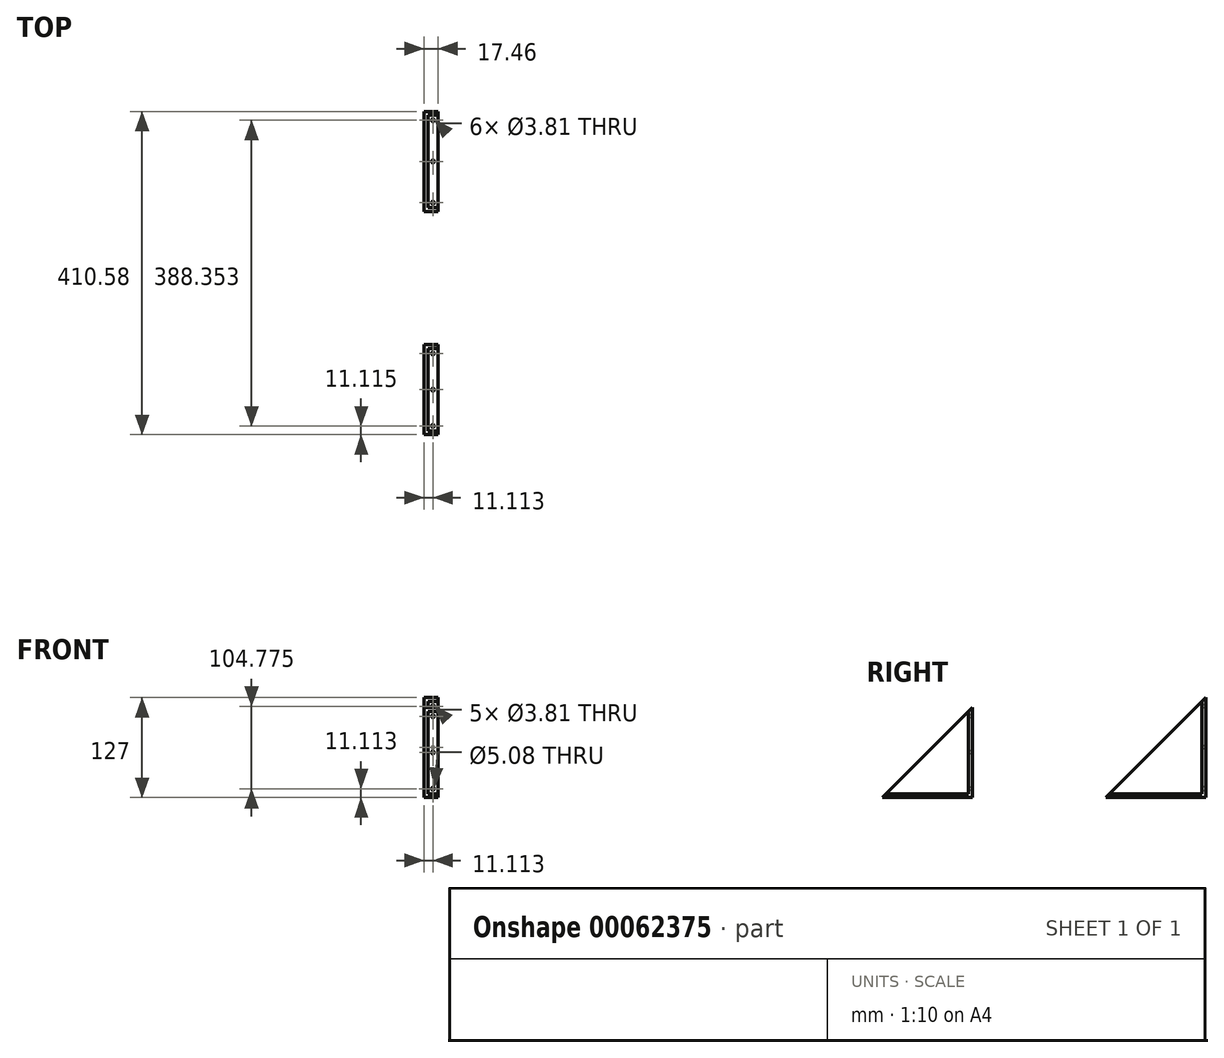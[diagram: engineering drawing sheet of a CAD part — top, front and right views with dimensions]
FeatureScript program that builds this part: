
annotation { "Feature Type Name" : "Feature", "Feature Type Description" : "" }
export const myFeature = defineFeature(function(context is Context, id is Id, definition is map)
    precondition{}
    {
        {
            var Q0;
            Q0=qCreatedBy(makeId("Right.planeOp"),FACE);
            var sketch = newSketch(context, id + "F0", { "sketchPlane" : qUnion([Q0])});
            skLineSegment(sketch, "E0", {"start": v(0, 0) * mm, "end": v(127, 127) * mm});
            skLineSegment(sketch, "E1", {"start": v(127, 127) * mm, "end": v(127, 0) * mm});
            skLineSegment(sketch, "E2", {"start": v(127, 0) * mm, "end": v(0, 0) * mm});
            skSolve(sketch);
        }
        {
            var Q0;
            Q0=makeQuery(id+"F0.imprint","IMPRINT",FACE,{"disambiguationData":[TD([[makeQuery(id+"F0.imprint","IMPRINT",EDGE,{"derivedFrom":sQuery(id+"F0.wireOp",EDGE,"E0")}),-1.0]])]});
            extrude(context, id + "F1", {"entities" : qUnion([Q0]), "depth" : 4.76 * mm});
        }
        {
            var Q0;
            Q0=makeQuery(id+"F1.opExtrude","CAP_FACE",FACE,{"disambiguationData":[OSD([sQuery(id+"F0.wireOp",EDGE,"E0"),sQuery(id+"F0.wireOp",EDGE,"E1"),sQuery(id+"F0.wireOp",EDGE,"E2")])],"isStart":false});
            var sketch = newSketch(context, id + "F2", { "sketchPlane" : qUnion([Q0])});
            skLineSegment(sketch, "E3", {"start": v(127, 4.76) * mm, "end": v(4.76, 4.76) * mm});
            skLineSegment(sketch, "E4", {"start": v(122.24, 4.76) * mm, "end": v(122.24, 122.24) * mm});
            skSolve(sketch);
        }
        {
            var Q0;
            {var subQ3=sQuery(id+"F2.wireOp",EDGE,"E4");Q0=makeQuery(id+"F2.imprint","IMPRINT",FACE,{"disambiguationData":[TD([[makeQuery(id+"F2.imprint","IMPRINT",EDGE,{"derivedFrom":subQ3}),-1.0]])]});}
            var Q1;
            {var subQ0=makeQuery(id+"F1.opExtrude","CAP_EDGE",EDGE,{"disambiguationData":[OSD([sQuery(id+"F0.wireOp",EDGE,"E2")])],"isStart":false});Q1=makeQuery(id+"F2.imprint","IMPRINT",FACE,{"disambiguationData":[TD([[makeQuery(id+"F2.imprint","IMPRINT",EDGE,{"derivedFrom":subQ0}),-1.0]])]});}
            extrude(context, id + "F3", {"entities" : qUnion([Q0, Q1]), "operationType" : NewBodyOperationType.ADD, "depth" : 12.7 * mm});
        }
        {
            var Q0;
            Q0=makeQuery(id+"F3.opExtrude","SWEPT_FACE",FACE,{"disambiguationData":[OSD([sQuery(id+"F2.wireOp",EDGE,"E3")])]});
            var sketch = newSketch(context, id + "F4", { "sketchPlane" : qUnion([Q0])});
            skCircle(sketch, "E5", {"center": v(11.11, 11.11) * mm, "radius": 1.9 * mm});
            skPoint(sketch, "E5.centerSnap0", {"position": v(11.11, 4.76) * mm});
            skCircle(sketch, "E6", {"center": v(11.11, 115.89) * mm, "radius": 1.9 * mm});
            skCircle(sketch, "E7", {"center": v(11.11, 63.5) * mm, "radius": 1.9 * mm});
            skPoint(sketch, "E7.centerSnap0", {"position": v(17.46, 63.5) * mm});
            skSolve(sketch);
        }
        {
            var Q0;
            Q0=qSketchRegion(id+"F4",true);
            extrude(context, id + "F5", {"entities" : qUnion([Q0]), "operationType" : NewBodyOperationType.REMOVE, "endBound" : BoundingType.UP_TO_NEXT, "oppositeDirection" : true, "depth" : 25.4 * mm});
        }
        {
            var Q0;
            Q0=makeQuery(id+"F3.opExtrude","SWEPT_FACE",FACE,{"disambiguationData":[OSD([sQuery(id+"F2.wireOp",EDGE,"E4")])]});
            var sketch = newSketch(context, id + "F6", { "sketchPlane" : qUnion([Q0])});
            skCircle(sketch, "E8", {"center": v(11.11, 115.89) * mm, "radius": 1.9 * mm});
            skPoint(sketch, "E8.centerSnap0", {"position": v(11.11, 122.24) * mm});
            skCircle(sketch, "E9", {"center": v(11.11, 11.11) * mm, "radius": 2.54 * mm});
            skCircle(sketch, "E10", {"center": v(11.11, 63.5) * mm, "radius": 1.9 * mm});
            skPoint(sketch, "E10.centerSnap0", {"position": v(17.46, 63.5) * mm});
            skSolve(sketch);
        }
        {
            var Q0;
            Q0=makeQuery(id+"F6.imprint","IMPRINT",FACE,{"disambiguationData":[TD([[makeQuery(id+"F6.imprint","IMPRINT",EDGE,{"derivedFrom":sQuery(id+"F6.wireOp",EDGE,"E8")}),1.0]])]});
            var Q1;
            Q1=makeQuery(id+"F6.imprint","IMPRINT",FACE,{"disambiguationData":[TD([[makeQuery(id+"F6.imprint","IMPRINT",EDGE,{"derivedFrom":sQuery(id+"F6.wireOp",EDGE,"E9")}),1.0]])]});
            var Q2;
            Q2=makeQuery(id+"F6.imprint","IMPRINT",FACE,{"disambiguationData":[TD([[makeQuery(id+"F6.imprint","IMPRINT",EDGE,{"derivedFrom":sQuery(id+"F6.wireOp",EDGE,"E10")}),1.0]])]});
            extrude(context, id + "F7", {"entities" : qUnion([Q0, Q1, Q2]), "operationType" : NewBodyOperationType.REMOVE, "endBound" : BoundingType.UP_TO_NEXT, "oppositeDirection" : true, "depth" : 25.4 * mm});
        }
        {
            var Q0;
            Q0=qCreatedBy(makeId("Right.planeOp"),FACE);
            var sketch = newSketch(context, id + "F8", { "sketchPlane" : qUnion([Q0])});
            skLineSegment(sketch, "E11", {"start": v(-283.58, 0) * mm, "end": v(-169.28, 114.3) * mm});
            skLineSegment(sketch, "E12", {"start": v(-169.28, 114.3) * mm, "end": v(-169.28, 0) * mm});
            skLineSegment(sketch, "E13", {"start": v(-169.28, 0) * mm, "end": v(-283.58, 0) * mm});
            skSolve(sketch);
        }
        {
            var Q0;
            Q0=makeQuery(id+"F8.imprint","IMPRINT",FACE,{"disambiguationData":[TD([[makeQuery(id+"F8.imprint","IMPRINT",EDGE,{"derivedFrom":sQuery(id+"F8.wireOp",EDGE,"E11")}),-1.0]])]});
            extrude(context, id + "F9", {"entities" : qUnion([Q0]), "depth" : 4.76 * mm});
        }
        {
            var Q0;
            Q0=makeQuery(id+"F9.opExtrude","CAP_FACE",FACE,{"disambiguationData":[OSD([sQuery(id+"F8.wireOp",EDGE,"E11"),sQuery(id+"F8.wireOp",EDGE,"E12"),sQuery(id+"F8.wireOp",EDGE,"E13")])],"isStart":false});
            var sketch = newSketch(context, id + "F10", { "sketchPlane" : qUnion([Q0])});
            skLineSegment(sketch, "E14", {"start": v(-278.82, 4.76) * mm, "end": v(-169.28, 4.76) * mm});
            skLineSegment(sketch, "E15", {"start": v(-174.04, 4.76) * mm, "end": v(-174.04, 109.54) * mm});
            skSolve(sketch);
        }
        {
            var Q0;
            {var subQ3=sQuery(id+"F10.wireOp",EDGE,"E15");Q0=makeQuery(id+"F10.imprint","IMPRINT",FACE,{"disambiguationData":[TD([[makeQuery(id+"F10.imprint","IMPRINT",EDGE,{"derivedFrom":subQ3}),-1.0]])]});}
            var Q1;
            {var subQ0=makeQuery(id+"F9.opExtrude","CAP_EDGE",EDGE,{"disambiguationData":[OSD([sQuery(id+"F8.wireOp",EDGE,"E13")])],"isStart":false});Q1=makeQuery(id+"F10.imprint","IMPRINT",FACE,{"disambiguationData":[TD([[makeQuery(id+"F10.imprint","IMPRINT",EDGE,{"derivedFrom":subQ0}),-1.0]])]});}
            extrude(context, id + "F11", {"entities" : qUnion([Q0, Q1]), "operationType" : NewBodyOperationType.ADD, "depth" : 12.7 * mm});
        }
        {
            var Q0;
            Q0=makeQuery(id+"F11.opExtrude","SWEPT_FACE",FACE,{"disambiguationData":[OSD([sQuery(id+"F10.wireOp",EDGE,"E14")])]});
            var sketch = newSketch(context, id + "F12", { "sketchPlane" : qUnion([Q0])});
            skCircle(sketch, "E16", {"center": v(11.11, -272.47) * mm, "radius": 1.9 * mm});
            skPoint(sketch, "E16.centerSnap0", {"position": v(11.11, -278.82) * mm});
            skCircle(sketch, "E17", {"center": v(11.11, -180.4) * mm, "radius": 1.9 * mm});
            skPoint(sketch, "E17.centerSnap0", {"position": v(11.11, -174.04) * mm});
            skCircle(sketch, "E18", {"center": v(11.11, -226.43) * mm, "radius": 1.9 * mm});
            skPoint(sketch, "E18.centerSnap0", {"position": v(17.46, -226.43) * mm});
            skSolve(sketch);
        }
        {
            var Q0;
            Q0=makeQuery(id+"F12.imprint","IMPRINT",FACE,{"disambiguationData":[TD([[makeQuery(id+"F12.imprint","IMPRINT",EDGE,{"derivedFrom":sQuery(id+"F12.wireOp",EDGE,"E16")}),1.0]])]});
            var Q1;
            Q1=makeQuery(id+"F12.imprint","IMPRINT",FACE,{"disambiguationData":[TD([[makeQuery(id+"F12.imprint","IMPRINT",EDGE,{"derivedFrom":sQuery(id+"F12.wireOp",EDGE,"E18")}),1.0]])]});
            var Q2;
            Q2=makeQuery(id+"F12.imprint","IMPRINT",FACE,{"disambiguationData":[TD([[makeQuery(id+"F12.imprint","IMPRINT",EDGE,{"derivedFrom":sQuery(id+"F12.wireOp",EDGE,"E17")}),1.0]])]});
            extrude(context, id + "F13", {"entities" : qUnion([Q0, Q1, Q2]), "operationType" : NewBodyOperationType.REMOVE, "endBound" : BoundingType.UP_TO_NEXT, "oppositeDirection" : true, "depth" : 25.4 * mm});
        }
        {
            var Q0;
            Q0=makeQuery(id+"F11.opExtrude","SWEPT_FACE",FACE,{"disambiguationData":[OSD([sQuery(id+"F10.wireOp",EDGE,"E15")])]});
            var sketch = newSketch(context, id + "F14", { "sketchPlane" : qUnion([Q0])});
            skCircle(sketch, "E19", {"center": v(11.11, 103.19) * mm, "radius": 1.9 * mm});
            skPoint(sketch, "E19.centerSnap0", {"position": v(11.11, 109.54) * mm});
            skCircle(sketch, "E20", {"center": v(11.11, 11.11) * mm, "radius": 1.9 * mm});
            skPoint(sketch, "E20.centerSnap0", {"position": v(11.11, 4.76) * mm});
            skCircle(sketch, "E21", {"center": v(11.11, 57.15) * mm, "radius": 1.9 * mm});
            skPoint(sketch, "E21.centerSnap0", {"position": v(4.76, 57.15) * mm});
            skSolve(sketch);
        }
        {
            var Q0;
            Q0=qSketchRegion(id+"F14",true);
            extrude(context, id + "F15", {"entities" : qUnion([Q0]), "operationType" : NewBodyOperationType.REMOVE, "endBound" : BoundingType.UP_TO_NEXT, "oppositeDirection" : true, "depth" : 25.4 * mm});
        }
    });
